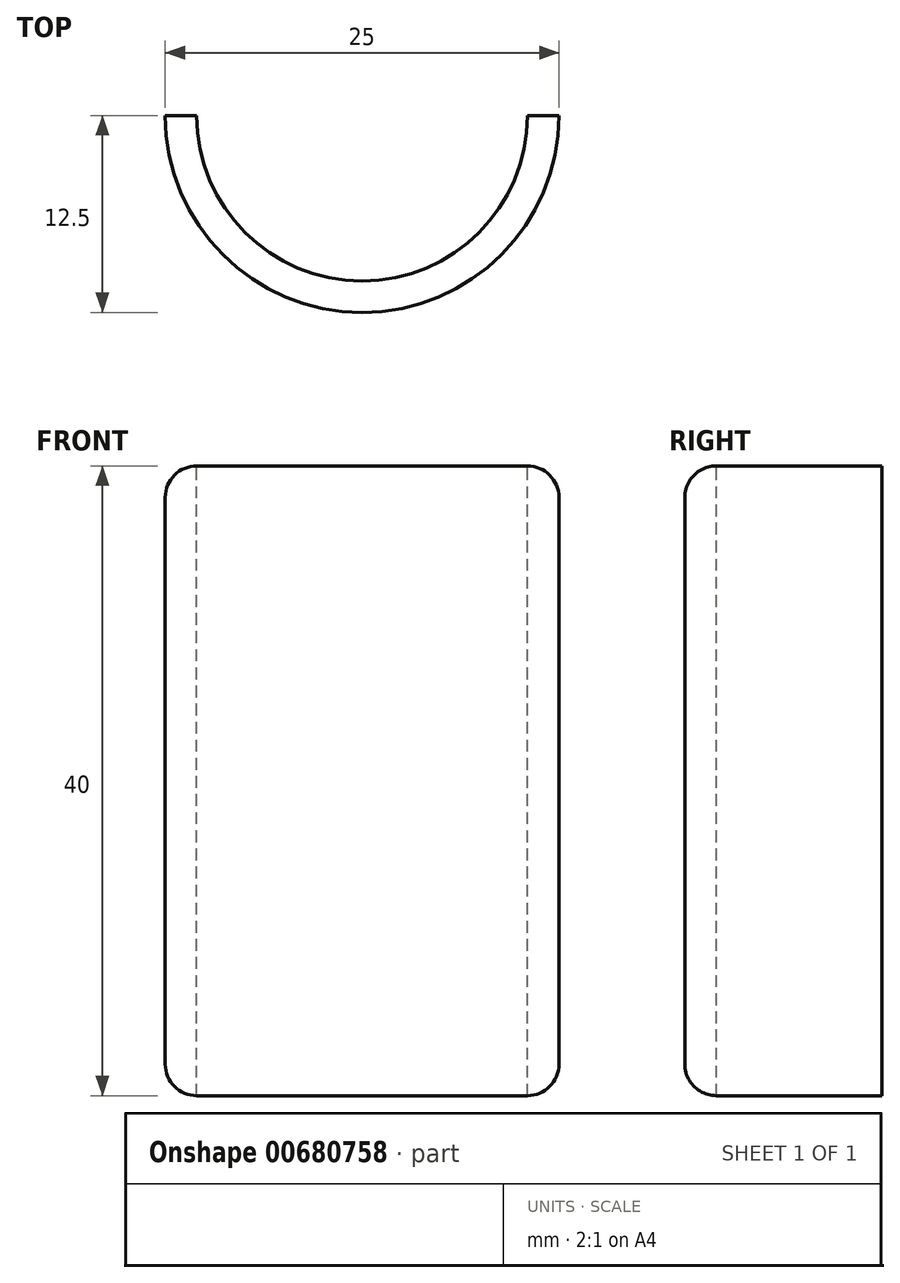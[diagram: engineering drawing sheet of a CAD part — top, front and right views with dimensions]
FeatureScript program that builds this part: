
annotation { "Feature Type Name" : "Feature", "Feature Type Description" : "" }
export const myFeature = defineFeature(function(context is Context, id is Id, definition is map)
    precondition{}
    {
        {
            var Q0;
            Q0=qCreatedBy(makeId("Front.planeOp"),FACE);
            var sketch = newSketch(context, id + "F0", { "sketchPlane" : qUnion([Q0])});
            skLineSegment(sketch, "E0.bottom", {"start": v(-4.25, 20) * mm, "end": v(6.25, 20) * mm});
            skLineSegment(sketch, "E0.top", {"start": v(-4.25, -20) * mm, "end": v(6.25, -20) * mm});
            skLineSegment(sketch, "E0.left", {"start": v(-6.25, 18) * mm, "end": v(-6.25, -18) * mm});
            skLineSegment(sketch, "E0.right", {"start": v(6.25, 20) * mm, "end": v(6.25, -20) * mm});
            skPoint(sketch, "E0.middle", {"position": v(0, 0) * mm});
            skPoint(sketch, "E1.visualSharp", {"position": v(-6.25, 20) * mm});
            skArc(sketch, "E1.filletArc", {"start": v(-4.25, 20) * mm, "mid": v(-5.66, 19.41) * mm, "end": v(-6.25, 18) * mm});
            skPoint(sketch, "E2.visualSharp", {"position": v(-6.25, -20) * mm});
            skArc(sketch, "E2.filletArc", {"start": v(-6.25, -18) * mm, "mid": v(-5.66, -19.41) * mm, "end": v(-4.25, -20) * mm});
            skSolve(sketch);
        }
        {
            var Q0;
            Q0=makeQuery(id+"F0.imprint","IMPRINT",FACE,{"disambiguationData":[TD([[makeQuery(id+"F0.imprint","IMPRINT",EDGE,{"derivedFrom":sQuery(id+"F0.wireOp",EDGE,"E0.bottom")}),-1.0]])]});
            var Q1;
            Q1=sQuery(id+"F0.wireOp",EDGE,"E0.right");
            revolve(context, id + "F1", {"entities" : qUnion([Q0]), "axis" : qUnion([Q1]), "revolveType" : RevolveType.ONE_DIRECTION, "angle" : 180 * degree});
        }
        {
            var Q0;
            Q0=makeQuery(id+"F1.opRevolve","SWEPT_FACE",FACE,{"disambiguationData":[OSD([sQuery(id+"F0.wireOp",EDGE,"E0.bottom")])]});
            var sketch = newSketch(context, id + "F2", { "sketchPlane" : qUnion([Q0])});
            skCircle(sketch, "E3", {"center": v(6.25, 0) * mm, "radius": 10.5 * mm});
            skLineSegment(sketch, "E4", {"start": v(-4.25, 0) * mm, "end": v(16.75, 0) * mm});
            skSolve(sketch);
        }
        {
            var Q0;
            Q0=qSketchRegion(id+"F2",true);
            extrude(context, id + "F3", {"entities" : qUnion([Q0]), "operationType" : NewBodyOperationType.REMOVE, "oppositeDirection" : true, "depth" : 40 * mm, "offsetDistance" : 25 * mm});
        }
        {
            var Q0;
            Q0=makeQuery(id+"F1.opRevolve","SWEPT_BODY",BODY,{"disambiguationData":[OSD([sQuery(id+"F0.wireOp",EDGE,"E0.bottom"),sQuery(id+"F0.wireOp",EDGE,"E0.top"),sQuery(id+"F0.wireOp",EDGE,"E0.left"),sQuery(id+"F0.wireOp",EDGE,"E0.right"),sQuery(id+"F0.wireOp",EDGE,"E1.filletArc"),sQuery(id+"F0.wireOp",EDGE,"E2.filletArc")])]});
            var Q1;
            Q1=qCreatedBy(makeId("Front.planeOp"),FACE);
            mirror(context, id + "F4", {"entities" : qUnion([Q0]), "mirrorPlane" : qUnion([Q1])});
        }
        {
            var Q0;
            Q0=makeQuery(id+"F1.opRevolve","SWEPT_BODY",BODY,{"disambiguationData":[OSD([sQuery(id+"F0.wireOp",EDGE,"E0.bottom"),sQuery(id+"F0.wireOp",EDGE,"E0.top"),sQuery(id+"F0.wireOp",EDGE,"E0.left"),sQuery(id+"F0.wireOp",EDGE,"E0.right"),sQuery(id+"F0.wireOp",EDGE,"E1.filletArc"),sQuery(id+"F0.wireOp",EDGE,"E2.filletArc")])]});
            deleteBodies(context, id + "F5", {"entities" : qUnion([Q0])});
        }
    });
